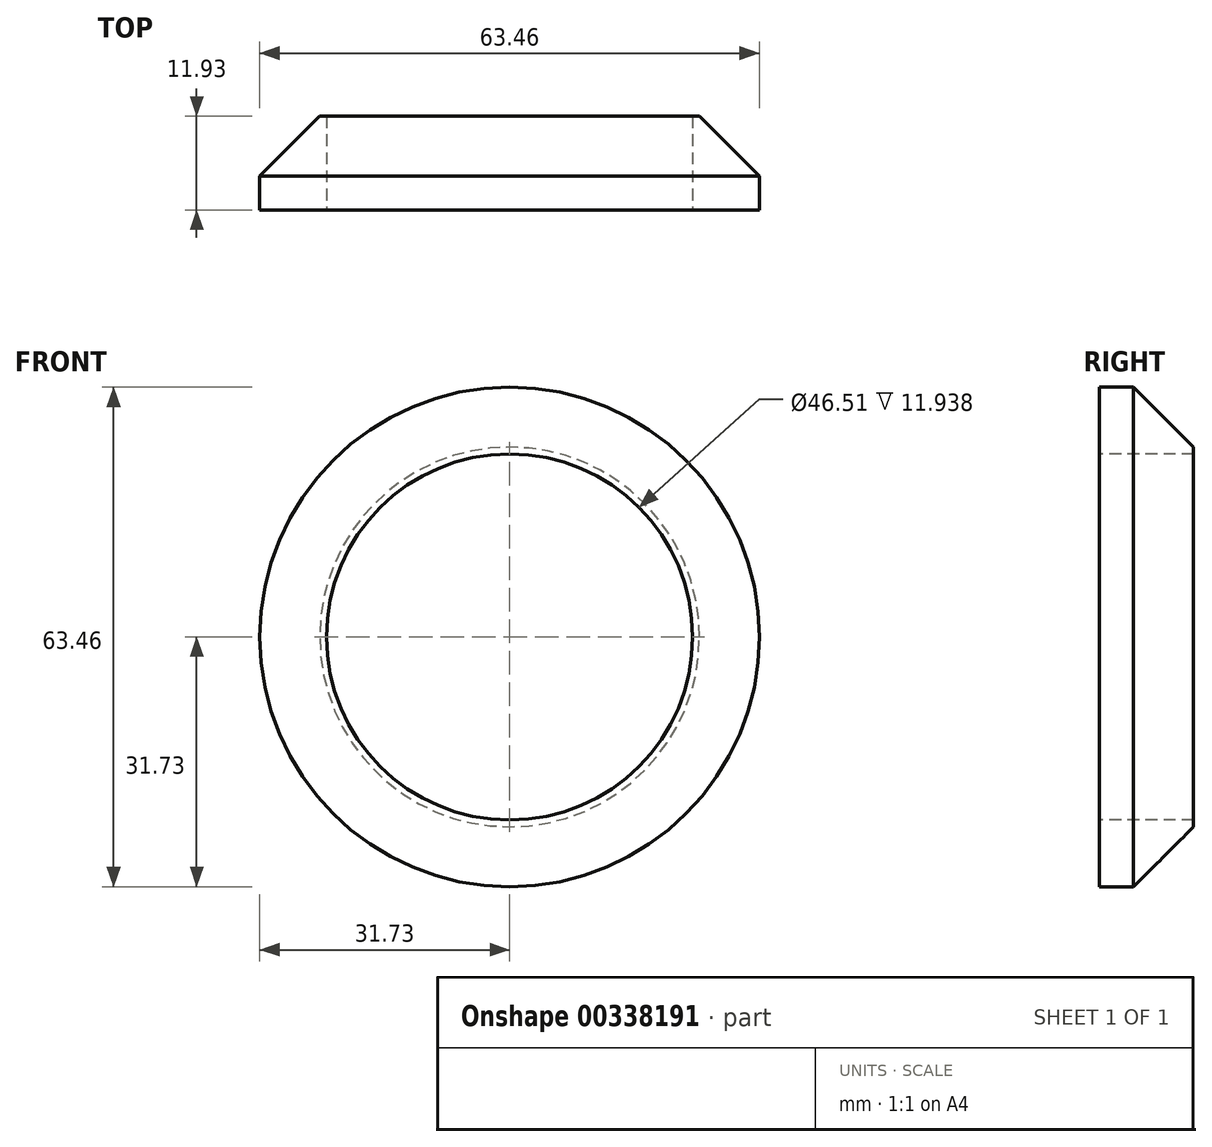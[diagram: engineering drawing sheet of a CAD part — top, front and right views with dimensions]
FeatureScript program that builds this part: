
annotation { "Feature Type Name" : "Feature", "Feature Type Description" : "" }
export const myFeature = defineFeature(function(context is Context, id is Id, definition is map)
    precondition{}
    {
        {
            var Q0;
            Q0=qCreatedBy(makeId("Top.planeOp"),FACE);
            var sketch = newSketch(context, id + "F0", { "sketchPlane" : qUnion([Q0])});
            skLineSegment(sketch, "E0", {"start": v(0, 57.33) * mm, "end": v(-7.82, 49.66) * mm});
            skLineSegment(sketch, "E1", {"start": v(-7.82, 49.66) * mm, "end": v(-11.19, 49.66) * mm});
            skLineSegment(sketch, "E2", {"start": v(-11.19, 49.66) * mm, "end": v(-15.79, 46.29) * mm});
            skLineSegment(sketch, "E3", {"start": v(-15.79, 46.29) * mm, "end": v(-7.51, 46.29) * mm});
            skLineSegment(sketch, "E4", {"start": v(-7.51, 46.29) * mm, "end": v(-20.08, 39.85) * mm});
            skLineSegment(sketch, "E5", {"start": v(-20.08, 39.85) * mm, "end": v(-26.52, 34.64) * mm});
            skLineSegment(sketch, "E6", {"start": v(-26.52, 34.64) * mm, "end": v(-23.83, 31.32) * mm});
            skLineSegment(sketch, "E7", {"start": v(-23.83, 31.32) * mm, "end": v(-19.16, 31.32) * mm});
            skLineSegment(sketch, "E8", {"start": v(-19.16, 31.32) * mm, "end": v(-15.79, 31.32) * mm});
            skLineSegment(sketch, "E9", {"start": v(-15.79, 31.32) * mm, "end": v(-15.79, 27.28) * mm});
            skLineSegment(sketch, "E10", {"start": v(-15.79, 27.28) * mm, "end": v(-22.22, 24.52) * mm});
            skLineSegment(sketch, "E11", {"start": v(-22.22, 24.52) * mm, "end": v(-27.13, 24.52) * mm});
            skLineSegment(sketch, "E12", {"start": v(-27.13, 24.52) * mm, "end": v(-35.4, 19) * mm});
            skLineSegment(sketch, "E13", {"start": v(-35.4, 19) * mm, "end": v(-39.4, 19) * mm});
            skLineSegment(sketch, "E14", {"start": v(-39.4, 19) * mm, "end": v(-39.4, 14.4) * mm});
            skLineSegment(sketch, "E15", {"start": v(-39.4, 14.4) * mm, "end": v(-28.97, 14.4) * mm});
            skLineSegment(sketch, "E16", {"start": v(-28.97, 14.4) * mm, "end": v(-19.16, 14.4) * mm});
            skLineSegment(sketch, "E17", {"start": v(-19.16, 14.4) * mm, "end": v(-11.19, 14.4) * mm});
            skLineSegment(sketch, "E18", {"start": v(-11.19, 14.4) * mm, "end": v(-21.92, 5.82) * mm});
            skLineSegment(sketch, "E19", {"start": v(-21.92, 5.82) * mm, "end": v(-31.73, 5.82) * mm});
            skLineSegment(sketch, "E20", {"start": v(-31.73, 5.82) * mm, "end": v(-43.68, 8.58) * mm});
            skLineSegment(sketch, "E21", {"start": v(-43.68, 8.58) * mm, "end": v(-47.98, 4.9) * mm});
            skLineSegment(sketch, "E22", {"start": v(-47.98, 4.9) * mm, "end": v(-43.07, 4.9) * mm});
            skLineSegment(sketch, "E23", {"start": v(-43.07, 4.9) * mm, "end": v(-43.07, 0) * mm});
            skLineSegment(sketch, "E24", {"start": v(-43.07, 0) * mm, "end": v(-46.14, 0) * mm});
            skLineSegment(sketch, "E25", {"start": v(-46.14, 0) * mm, "end": v(-38.17, -3.37) * mm});
            skLineSegment(sketch, "E26", {"start": v(-38.17, -3.37) * mm, "end": v(-35.4, -3.37) * mm});
            skLineSegment(sketch, "E27", {"start": v(-35.4, -3.37) * mm, "end": v(-19.16, -5.82) * mm});
            skLineSegment(sketch, "E28", {"start": v(-19.16, -5.82) * mm, "end": v(-11.19, -5.82) * mm});
            skLineSegment(sketch, "E29", {"start": v(-11.19, -5.82) * mm, "end": v(-8.43, -5.82) * mm});
            skLineSegment(sketch, "E30", {"start": v(-8.43, -5.82) * mm, "end": v(-14.56, -8.9) * mm});
            skLineSegment(sketch, "E31", {"start": v(-14.56, -8.9) * mm, "end": v(-25.6, -8.9) * mm});
            skLineSegment(sketch, "E32", {"start": v(-25.6, -8.9) * mm, "end": v(-35.4, -8.9) * mm});
            skLineSegment(sketch, "E33", {"start": v(-35.4, -8.9) * mm, "end": v(-42.76, -12.57) * mm});
            skLineSegment(sketch, "E34", {"start": v(-42.76, -12.57) * mm, "end": v(-43.68, -10.73) * mm});
            skLineSegment(sketch, "E35", {"start": v(-43.68, -10.73) * mm, "end": v(-51.65, -10.73) * mm});
            skLineSegment(sketch, "E36", {"start": v(-51.65, -10.73) * mm, "end": v(-55.95, -15.02) * mm});
            skLineSegment(sketch, "E37", {"start": v(-55.95, -15.02) * mm, "end": v(-46.44, -20.85) * mm});
            skLineSegment(sketch, "E38", {"start": v(-46.44, -20.85) * mm, "end": v(-35.4, -20.85) * mm});
            skLineSegment(sketch, "E39", {"start": v(-35.4, -20.85) * mm, "end": v(-19.16, -20.85) * mm});
            skLineSegment(sketch, "E40", {"start": v(-19.16, -20.85) * mm, "end": v(-11.19, -18.4) * mm});
            skLineSegment(sketch, "E41", {"start": v(-11.19, -18.4) * mm, "end": v(-6.9, -21.46) * mm});
            skLineSegment(sketch, "E42", {"start": v(-6.9, -21.46) * mm, "end": v(-11.19, -27.47) * mm});
            skLineSegment(sketch, "E43", {"start": v(-11.19, -27.47) * mm, "end": v(-23.76, -27.47) * mm});
            skLineSegment(sketch, "E44", {"start": v(-23.76, -27.47) * mm, "end": v(-32.34, -29.74) * mm});
            skLineSegment(sketch, "E45", {"start": v(-32.34, -29.74) * mm, "end": v(-47.98, -27.28) * mm});
            skLineSegment(sketch, "E46", {"start": v(-47.98, -27.28) * mm, "end": v(-51.96, -30.35) * mm});
            skLineSegment(sketch, "E47", {"start": v(-51.96, -30.35) * mm, "end": v(-61.16, -34.64) * mm});
            skLineSegment(sketch, "E48", {"start": v(-61.16, -34.64) * mm, "end": v(-52.57, -42.3) * mm});
            skLineSegment(sketch, "E49", {"start": v(-52.57, -42.3) * mm, "end": v(-34.49, -45.98) * mm});
            skLineSegment(sketch, "E50", {"start": v(-34.49, -45.98) * mm, "end": v(-20.08, -43.22) * mm});
            skLineSegment(sketch, "E51", {"start": v(-20.08, -43.22) * mm, "end": v(-11.19, -45.98) * mm});
            skLineSegment(sketch, "E52", {"start": v(-11.19, -45.98) * mm, "end": v(0, -45.98) * mm});
            skSolve(sketch);
        }
        {
            var Q0;
            Q0=qCreatedBy(makeId("Top.planeOp"),FACE);
            var sketch = newSketch(context, id + "F1", { "sketchPlane" : qUnion([Q0])});
            skLineSegment(sketch, "E53", {"start": v(0, 57.63) * mm, "end": v(0, -47.2) * mm, "construction": true});
            skSolve(sketch);
        }
        {
            var Q0;
            Q0=sQuery(id+"F1.wireOp",EDGE,"E53");
            var Q1;
            Q1=sQuery(id+"F0.wireOp",EDGE,"E44");
            var Q2;
            Q2=sQuery(id+"F0.wireOp",EDGE,"E4");
            var Q3;
            Q3=sQuery(id+"F0.wireOp",EDGE,"E40");
            var Q4;
            Q4=sQuery(id+"F0.wireOp",EDGE,"E0");
            var Q5;
            Q5=sQuery(id+"F0.wireOp",EDGE,"E15");
            var Q6;
            Q6=sQuery(id+"F0.wireOp",EDGE,"E17");
            var Q7;
            Q7=sQuery(id+"F0.wireOp",EDGE,"E28");
            var Q8;
            Q8=sQuery(id+"F0.wireOp",EDGE,"E33");
            var Q9;
            Q9=sQuery(id+"F0.wireOp",EDGE,"E49");
            var Q10;
            Q10=sQuery(id+"F0.wireOp",EDGE,"E3");
            var Q11;
            Q11=sQuery(id+"F0.wireOp",EDGE,"E5");
            var Q12;
            Q12=sQuery(id+"F0.wireOp",EDGE,"E35");
            var Q13;
            Q13=sQuery(id+"F0.wireOp",EDGE,"E25");
            var Q14;
            Q14=sQuery(id+"F0.wireOp",EDGE,"E32");
            var Q15;
            Q15=sQuery(id+"F0.wireOp",EDGE,"E10");
            var Q16;
            Q16=sQuery(id+"F0.wireOp",EDGE,"E16");
            var Q17;
            Q17=sQuery(id+"F0.wireOp",EDGE,"E51");
            var Q18;
            Q18=sQuery(id+"F0.wireOp",EDGE,"E38");
            var Q19;
            Q19=sQuery(id+"F0.wireOp",EDGE,"E31");
            var Q20;
            Q20=sQuery(id+"F0.wireOp",EDGE,"E19");
            var Q21;
            Q21=sQuery(id+"F0.wireOp",EDGE,"E43");
            var Q22;
            Q22=sQuery(id+"F0.wireOp",EDGE,"E12");
            var Q23;
            Q23=sQuery(id+"F0.wireOp",EDGE,"E27");
            var Q24;
            Q24=sQuery(id+"F0.wireOp",EDGE,"E42");
            var Q25;
            Q25=sQuery(id+"F0.wireOp",EDGE,"E39");
            var Q26;
            Q26=sQuery(id+"F0.wireOp",EDGE,"E52");
            var Q27;
            Q27=sQuery(id+"F0.wireOp",EDGE,"E20");
            var Q28;
            Q28=sQuery(id+"F0.wireOp",EDGE,"E45");
            var Q29;
            Q29=sQuery(id+"F0.wireOp",EDGE,"E18");
            var Q30;
            Q30=sQuery(id+"F0.wireOp",EDGE,"E50");
            var Q31;
            Q31=sQuery(id+"F0.wireOp",EDGE,"E46");
            var Q32;
            Q32=sQuery(id+"F0.wireOp",EDGE,"E24");
            var Q33;
            Q33=sQuery(id+"F0.wireOp",EDGE,"E14");
            var Q34;
            Q34=sQuery(id+"F0.wireOp",EDGE,"E21");
            var Q35;
            Q35=sQuery(id+"F0.wireOp",EDGE,"E30");
            var Q36;
            Q36=sQuery(id+"F0.wireOp",EDGE,"E1");
            var Q37;
            Q37=sQuery(id+"F0.wireOp",EDGE,"E2");
            var Q38;
            Q38=sQuery(id+"F0.wireOp",EDGE,"E6");
            var Q39;
            Q39=sQuery(id+"F0.wireOp",EDGE,"E13");
            var Q40;
            Q40=sQuery(id+"F0.wireOp",EDGE,"E8");
            var Q41;
            Q41=sQuery(id+"F0.wireOp",EDGE,"E7");
            var Q42;
            Q42=sQuery(id+"F0.wireOp",EDGE,"E9");
            var Q43;
            Q43=sQuery(id+"F0.wireOp",EDGE,"E11");
            var Q44;
            Q44=sQuery(id+"F0.wireOp",EDGE,"E41");
            var Q45;
            Q45=sQuery(id+"F0.wireOp",EDGE,"E22");
            var Q46;
            Q46=sQuery(id+"F0.wireOp",EDGE,"E26");
            var Q47;
            Q47=sQuery(id+"F0.wireOp",EDGE,"E29");
            var Q48;
            Q48=sQuery(id+"F0.wireOp",EDGE,"E23");
            var Q49;
            Q49=sQuery(id+"F0.wireOp",EDGE,"E34");
            var Q50;
            Q50=sQuery(id+"F0.wireOp",EDGE,"E37");
            var Q51;
            Q51=sQuery(id+"F0.wireOp",EDGE,"E48");
            var Q52;
            Q52=sQuery(id+"F0.wireOp",EDGE,"E47");
            var Q53;
            Q53=sQuery(id+"F0.wireOp",EDGE,"E36");
            var Q54;
            Q54=sQuery(id+"F1.wireOp",EDGE,"E53");
            revolve(context, id + "F2", {"bodyType" : ToolBodyType.SURFACE, "surfaceEntities" : qUnion([Q0, Q1, Q2, Q3, Q4, Q5, Q6, Q7, Q8, Q9, Q10, Q11, Q12, Q13, Q14, Q15, Q16, Q17, Q18, Q19, Q20, Q21, Q22, Q23, Q24, Q25, Q26, Q27, Q28, Q29, Q30, Q31, Q32, Q33, Q34, Q35, Q36, Q37, Q38, Q39, Q40, Q41, Q42, Q43, Q44, Q45, Q46, Q47, Q48, Q49, Q50, Q51, Q52, Q53]), "axis" : qUnion([Q54]), "revolveType" : RevolveType.FULL});
        }
        {
            var Q0;
            Q0=makeQuery(id+"F2.opRevolve","SWEPT_EDGE",EDGE,{"disambiguationData":[OSD([sQuery(id+"F0.wireOp",VERTEX,"E42.end")])]});
            fillet(context, id + "F3", {"entities" : qUnion([Q0]), "radius" : 12.7 * mm, "tangentPropagation" : true, "allowEdgeOverflow" : false});
        }
        {
            var Q0;
            Q0=makeQuery(id+"F2.opRevolve","SWEPT_EDGE",EDGE,{"disambiguationData":[OSD([sQuery(id+"F0.wireOp",VERTEX,"E46.start")])]});
            var Q1;
            Q1=makeQuery(id+"F2.opRevolve","SWEPT_FACE",FACE,{"disambiguationData":[OSD([sQuery(id+"F0.wireOp",EDGE,"E37")])]});
            fillet(context, id + "F4", {"entities" : qUnion([Q0, Q1]), "radius" : 0.1 * mm, "tangentPropagation" : true, "allowEdgeOverflow" : false});
        }
        {
            var Q0;
            Q0=makeQuery(id+"F2.opRevolve","SWEPT_FACE",FACE,{"disambiguationData":[OSD([sQuery(id+"F0.wireOp",EDGE,"E18")])]});
            fillet(context, id + "F5", {"entities" : qUnion([Q0]), "radius" : 3.8 * mm, "tangentPropagation" : true, "allowEdgeOverflow" : false});
        }
        {
            var Q0;
            Q0=makeQuery(id+"F2.opRevolve","SWEPT_EDGE",EDGE,{"disambiguationData":[OSD([sQuery(id+"F0.wireOp",VERTEX,"E9.end")])]});
            fillet(context, id + "F6", {"entities" : qUnion([Q0]), "radius" : 5.08 * mm, "tangentPropagation" : true, "allowEdgeOverflow" : false});
        }
        {
            var Q0;
            Q0=makeQuery(id+"F2.opRevolve","SWEPT_EDGE",EDGE,{"disambiguationData":[OSD([sQuery(id+"F0.wireOp",VERTEX,"E2.end")])]});
            fillet(context, id + "F7", {"entities" : qUnion([Q0]), "radius" : 2.54 * mm, "allowEdgeOverflow" : false});
        }
        {
            var Q0;
            Q0=makeQuery(id+"F2.opRevolve","SWEPT_EDGE",EDGE,{"disambiguationData":[OSD([sQuery(id+"F0.wireOp",VERTEX,"E5.start")])]});
            chamfer(context, id + "F8", {"entities" : qUnion([Q0]), "width" : 2.54 * mm, "tangentPropagation" : true});
        }
        {
            var Q0;
            Q0=makeQuery(id+"F2.opRevolve","SWEPT_EDGE",EDGE,{"disambiguationData":[OSD([sQuery(id+"F0.wireOp",VERTEX,"E5.start")])]});
            var Q1;
            Q1=makeQuery(id+"F2.opRevolve","SWEPT_FACE",FACE,{"disambiguationData":[OSD([sQuery(id+"F0.wireOp",EDGE,"E4")])]});
            chamfer(context, id + "F9", {"entities" : qUnion([Q0, Q1]), "width" : 5.08 * mm, "tangentPropagation" : true});
        }
        {
            var Q0;
            Q0=makeQuery(id+"F2.opRevolve","SWEPT_FACE",FACE,{"disambiguationData":[OSD([sQuery(id+"F0.wireOp",EDGE,"E14")])]});
            fillet(context, id + "F10", {"entities" : qUnion([Q0]), "radius" : 1.27 * mm, "tangentPropagation" : true, "allowEdgeOverflow" : false});
        }
        {
            var Q0;
            Q0=makeQuery(id+"F2.opRevolve","SWEPT_EDGE",EDGE,{"disambiguationData":[OSD([sQuery(id+"F0.wireOp",VERTEX,"E6.start")])]});
            chamfer(context, id + "F11", {"entities" : qUnion([Q0]), "chamferType" : ChamferType.OFFSET_ANGLE, "width" : 2.54 * mm, "oppositeDirection" : false, "angle" : 60 * degree, "tangentPropagation" : true});
        }
        {
            var Q0;
            Q0=makeQuery(id+"F11.opChamfer","BLEND_EDGE",EDGE,{"blendedFrom":[makeQuery(id+"F2.opRevolve","SWEPT_EDGE",EDGE,{"disambiguationData":[OSD([sQuery(id+"F0.wireOp",VERTEX,"E6.start")])]}),makeQuery(id+"F2.opRevolve","SWEPT_FACE",FACE,{"disambiguationData":[OSD([sQuery(id+"F0.wireOp",EDGE,"E7"),sQuery(id+"F0.wireOp",EDGE,"E8")])]})],"blendedInto":[makeQuery(id+"F2.opRevolve","SWEPT_FACE",FACE,{"disambiguationData":[OSD([sQuery(id+"F0.wireOp",EDGE,"E7"),sQuery(id+"F0.wireOp",EDGE,"E8")])]})]});
            chamfer(context, id + "F12", {"entities" : qUnion([Q0]), "width" : 5.08 * mm, "tangentPropagation" : true});
        }
        {
            var Q0;
            Q0=makeQuery(id+"F2.opRevolve","SWEPT_EDGE",EDGE,{"disambiguationData":[OSD([sQuery(id+"F0.wireOp",VERTEX,"E24.end")])]});
            chamfer(context, id + "F13", {"entities" : qUnion([Q0]), "chamferType" : ChamferType.OFFSET_ANGLE, "width" : 2.54 * mm, "oppositeDirection" : false, "angle" : 15 * degree, "tangentPropagation" : true});
        }
        {
            var Q0;
            Q0=makeQuery(id+"F13.opChamfer","BLEND_EDGE",EDGE,{"blendedFrom":[makeQuery(id+"F2.opRevolve","SWEPT_EDGE",EDGE,{"disambiguationData":[OSD([sQuery(id+"F0.wireOp",VERTEX,"E24.end")])]}),makeQuery(id+"F2.opRevolve","SWEPT_FACE",FACE,{"disambiguationData":[OSD([sQuery(id+"F0.wireOp",EDGE,"E25")])]})],"blendedInto":[makeQuery(id+"F2.opRevolve","SWEPT_FACE",FACE,{"disambiguationData":[OSD([sQuery(id+"F0.wireOp",EDGE,"E25")])]})]});
            fillet(context, id + "F14", {"entities" : qUnion([Q0]), "radius" : 5.08 * mm, "tangentPropagation" : true, "allowEdgeOverflow" : false});
        }
        {
            var Q0;
            Q0=makeQuery(id+"F2.opRevolve","SWEPT_FACE",FACE,{"disambiguationData":[OSD([sQuery(id+"F0.wireOp",EDGE,"E19")])]});
            extrude(context, id + "F15", {"entities" : qUnion([Q0]), "oppositeDirection" : true, "depth" : 6.35 * mm, "hasSecondDirection" : true, "secondDirectionOppositeDirection" : false, "secondDirectionDepth" : 5.6 * mm});
        }
        {
            var Q0;
            Q0=makeQuery(id+"F15.opExtrude","CAP_EDGE",EDGE,{"disambiguationData":[OSD([sQuery(id+"F0.wireOp",VERTEX,"E20.start")])],"isStart":false});
            chamfer(context, id + "F16", {"entities" : qUnion([Q0]), "width" : 7.62 * mm, "tangentPropagation" : true});
        }
    });
